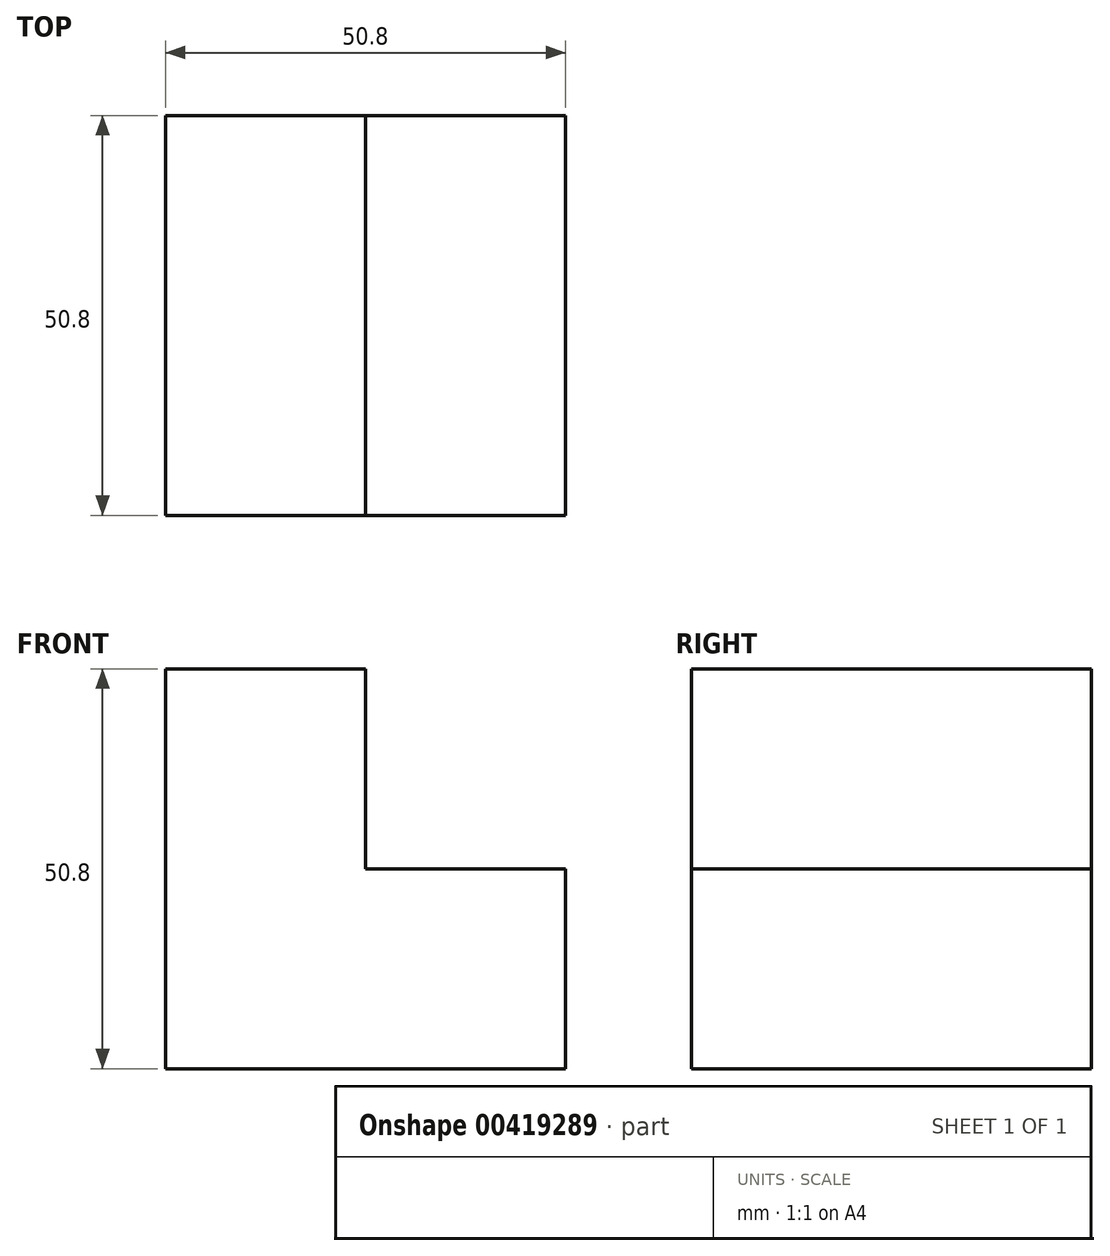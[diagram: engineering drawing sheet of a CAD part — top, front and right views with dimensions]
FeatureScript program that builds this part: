
annotation { "Feature Type Name" : "Feature", "Feature Type Description" : "" }
export const myFeature = defineFeature(function(context is Context, id is Id, definition is map)
    precondition{}
    {
        {
            var Q0;
            Q0=qCreatedBy(makeId("Front.planeOp"),FACE);
            var sketch = newSketch(context, id + "F0", { "sketchPlane" : qUnion([Q0])});
            skLineSegment(sketch, "E0", {"start": v(-50.8, 24) * mm, "end": v(-50.8, -26.8) * mm});
            skLineSegment(sketch, "E1", {"start": v(-50.8, -26.8) * mm, "end": v(0, -26.8) * mm});
            skLineSegment(sketch, "E2", {"start": v(0, -26.8) * mm, "end": v(0, -1.4) * mm});
            skLineSegment(sketch, "E3", {"start": v(0, -1.4) * mm, "end": v(-25.4, -1.4) * mm});
            skLineSegment(sketch, "E4", {"start": v(-25.4, -1.4) * mm, "end": v(-25.4, 24) * mm});
            skLineSegment(sketch, "E5", {"start": v(-25.4, 24) * mm, "end": v(-50.8, 24) * mm});
            skSolve(sketch);
        }
        {
            var Q0;
            Q0=makeQuery(id+"F0.imprint","IMPRINT",FACE,{"disambiguationData":[TD([[makeQuery(id+"F0.imprint","IMPRINT",EDGE,{"derivedFrom":sQuery(id+"F0.wireOp",EDGE,"E0")}),1.0]])]});
            extrude(context, id + "F1", {"entities" : qUnion([Q0]), "depth" : 50.8 * mm});
        }
    });
